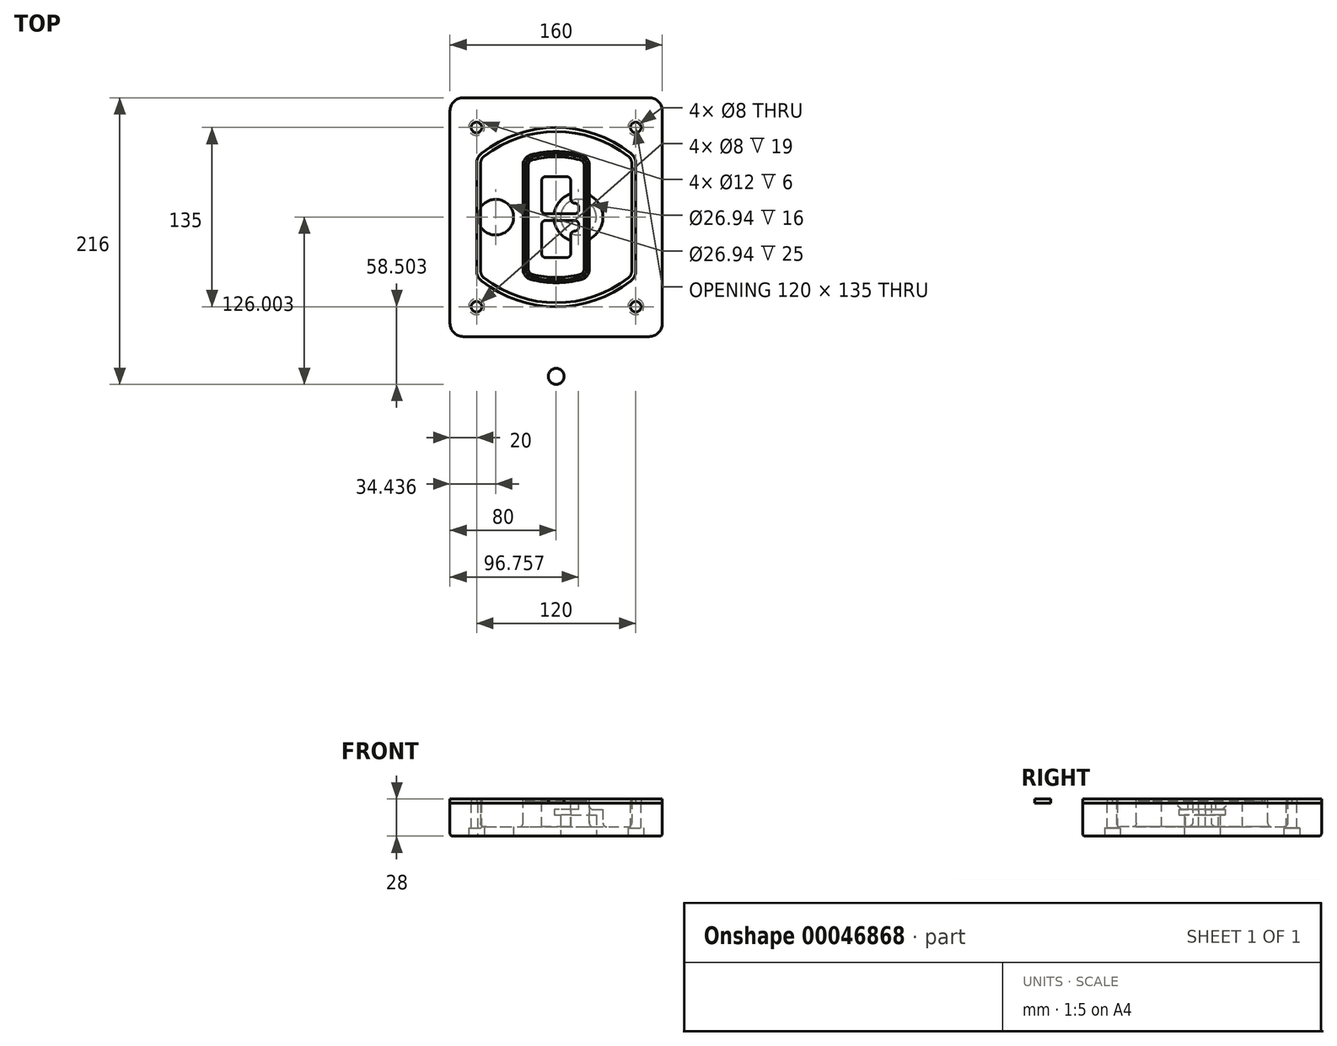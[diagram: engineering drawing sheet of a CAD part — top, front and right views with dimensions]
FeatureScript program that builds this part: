
annotation { "Feature Type Name" : "Feature", "Feature Type Description" : "" }
export const myFeature = defineFeature(function(context is Context, id is Id, definition is map)
    precondition{}
    {
        {
            var Q0;
            Q0=qCreatedBy(makeId("Top.planeOp"),FACE);
            var sketch = newSketch(context, id + "F0", { "sketchPlane" : qUnion([Q0])});
            skPoint(sketch, "E0.rect.middle", {"position": v(0, 0) * mm});
            skLineSegment(sketch, "E1.bottom", {"start": v(24.05, 28.38) * mm, "end": v(164.05, 28.38) * mm});
            skLineSegment(sketch, "E1.top", {"start": v(24.05, 208.38) * mm, "end": v(164.05, 208.38) * mm});
            skLineSegment(sketch, "E1.left", {"start": v(14.05, 38.38) * mm, "end": v(14.05, 198.38) * mm});
            skLineSegment(sketch, "E1.right", {"start": v(174.05, 38.38) * mm, "end": v(174.05, 198.38) * mm});
            skLineSegment(sketch, "E2", {"start": v(14.05, 208.38) * mm, "end": v(174.05, 28.38) * mm, "construction": true});
            skLineSegment(sketch, "E3", {"start": v(174.05, 208.38) * mm, "end": v(14.05, 28.38) * mm, "construction": true});
            skCircle(sketch, "E4", {"center": v(34.05, 185.88) * mm, "radius": 4 * mm});
            skCircle(sketch, "E5", {"center": v(154.05, 185.88) * mm, "radius": 4 * mm});
            skCircle(sketch, "E6", {"center": v(154.05, 50.88) * mm, "radius": 4 * mm});
            skCircle(sketch, "E7", {"center": v(34.05, 50.88) * mm, "radius": 4 * mm});
            skLineSegment(sketch, "E8", {"start": v(34.05, 185.88) * mm, "end": v(154.05, 185.88) * mm, "construction": true});
            skLineSegment(sketch, "E9", {"start": v(154.05, 185.88) * mm, "end": v(154.05, 50.88) * mm, "construction": true});
            skLineSegment(sketch, "E10", {"start": v(154.05, 50.88) * mm, "end": v(34.05, 50.88) * mm, "construction": true});
            skLineSegment(sketch, "E11", {"start": v(34.05, 50.88) * mm, "end": v(34.05, 185.88) * mm, "construction": true});
            skLineSegment(sketch, "E12", {"start": v(34.05, 158.68) * mm, "end": v(34.05, 78.09) * mm});
            skLineSegment(sketch, "E13", {"start": v(154.05, 158.68) * mm, "end": v(154.05, 78.09) * mm});
            skArc(sketch, "E14", {"start": v(150.2, 166.56) * mm, "mid": v(94.05, 185.88) * mm, "end": v(37.9, 166.56) * mm});
            skArc(sketch, "E15", {"start": v(37.9, 70.2) * mm, "mid": v(94.05, 50.88) * mm, "end": v(150.2, 70.2) * mm});
            skLineSegment(sketch, "E16", {"start": v(34.05, 118.38) * mm, "end": v(154.05, 118.38) * mm, "construction": true});
            skPoint(sketch, "E17.visualSharp", {"position": v(34.05, 73.38) * mm});
            skArc(sketch, "E17.filletArc", {"start": v(34.05, 78.09) * mm, "mid": v(35.06, 73.7) * mm, "end": v(37.9, 70.2) * mm});
            skPoint(sketch, "E18.visualSharp", {"position": v(34.05, 163.38) * mm});
            skArc(sketch, "E18.filletArc", {"start": v(37.9, 166.56) * mm, "mid": v(35.06, 163.06) * mm, "end": v(34.05, 158.68) * mm});
            skPoint(sketch, "E19.visualSharp", {"position": v(154.05, 163.38) * mm});
            skArc(sketch, "E19.filletArc", {"start": v(154.05, 158.68) * mm, "mid": v(153.04, 163.06) * mm, "end": v(150.2, 166.56) * mm});
            skPoint(sketch, "E20.visualSharp", {"position": v(154.05, 73.38) * mm});
            skArc(sketch, "E20.filletArc", {"start": v(150.2, 70.2) * mm, "mid": v(153.04, 73.7) * mm, "end": v(154.05, 78.09) * mm});
            skPoint(sketch, "E21.visualSharp", {"position": v(14.05, 208.38) * mm});
            skArc(sketch, "E21.filletArc", {"start": v(24.05, 208.38) * mm, "mid": v(16.98, 205.45) * mm, "end": v(14.05, 198.38) * mm});
            skPoint(sketch, "E22.visualSharp", {"position": v(174.05, 208.38) * mm});
            skArc(sketch, "E22.filletArc", {"start": v(174.05, 198.38) * mm, "mid": v(171.12, 205.45) * mm, "end": v(164.05, 208.38) * mm});
            skPoint(sketch, "E23.visualSharp", {"position": v(174.05, 28.38) * mm});
            skArc(sketch, "E23.filletArc", {"start": v(164.05, 28.38) * mm, "mid": v(171.12, 31.31) * mm, "end": v(174.05, 38.38) * mm});
            skPoint(sketch, "E24.visualSharp", {"position": v(14.05, 28.38) * mm});
            skArc(sketch, "E24.filletArc", {"start": v(14.05, 38.38) * mm, "mid": v(16.98, 31.31) * mm, "end": v(24.05, 28.38) * mm});
            skArc(sketch, "E25.0", {"start": v(151.05, 158.68) * mm, "mid": v(150.34, 161.75) * mm, "end": v(148.36, 164.2) * mm});
            skLineSegment(sketch, "E25.1", {"start": v(151.05, 158.68) * mm, "end": v(151.05, 78.09) * mm});
            skArc(sketch, "E25.2", {"start": v(148.36, 72.57) * mm, "mid": v(150.34, 75.02) * mm, "end": v(151.05, 78.09) * mm});
            skArc(sketch, "E25.3", {"start": v(39.74, 72.57) * mm, "mid": v(94.05, 53.88) * mm, "end": v(148.36, 72.57) * mm});
            skArc(sketch, "E25.4", {"start": v(37.05, 78.09) * mm, "mid": v(37.76, 75.02) * mm, "end": v(39.74, 72.57) * mm});
            skArc(sketch, "E25.5", {"start": v(148.36, 164.2) * mm, "mid": v(94.05, 182.88) * mm, "end": v(39.74, 164.2) * mm});
            skLineSegment(sketch, "E25.6", {"start": v(37.05, 158.68) * mm, "end": v(37.05, 78.09) * mm});
            skArc(sketch, "E25.7", {"start": v(39.74, 164.2) * mm, "mid": v(37.76, 161.75) * mm, "end": v(37.05, 158.68) * mm});
            skArc(sketch, "E26.0", {"start": v(35.43, 169.71) * mm, "mid": v(31.47, 164.82) * mm, "end": v(30.05, 158.68) * mm});
            skArc(sketch, "E26.1", {"start": v(152.67, 169.71) * mm, "mid": v(94.05, 189.88) * mm, "end": v(35.43, 169.71) * mm});
            skArc(sketch, "E26.2", {"start": v(158.05, 158.68) * mm, "mid": v(156.63, 164.82) * mm, "end": v(152.67, 169.71) * mm});
            skLineSegment(sketch, "E26.3", {"start": v(158.05, 158.68) * mm, "end": v(158.05, 78.09) * mm});
            skArc(sketch, "E26.4", {"start": v(152.67, 67.05) * mm, "mid": v(156.63, 71.95) * mm, "end": v(158.05, 78.09) * mm});
            skLineSegment(sketch, "E26.5", {"start": v(30.05, 158.68) * mm, "end": v(30.05, 78.09) * mm});
            skArc(sketch, "E26.6", {"start": v(35.43, 67.05) * mm, "mid": v(94.05, 46.88) * mm, "end": v(152.67, 67.05) * mm});
            skArc(sketch, "E26.7", {"start": v(30.05, 78.09) * mm, "mid": v(31.47, 71.95) * mm, "end": v(35.43, 67.05) * mm});
            skSolve(sketch);
        }
        {
            var Q0;
            Q0=makeQuery(id+"F0.imprint","IMPRINT",FACE,{"disambiguationData":[TD([[makeQuery(id+"F0.imprint","IMPRINT",EDGE,{"derivedFrom":sQuery(id+"F0.wireOp",EDGE,"E1.bottom")}),1.0]])]});
            var Q1;
            Q1=makeQuery(id+"F0.imprint","IMPRINT",FACE,{"disambiguationData":[TD([[makeQuery(id+"F0.imprint","IMPRINT",EDGE,{"derivedFrom":sQuery(id+"F0.wireOp",EDGE,"E12")}),1.0]])]});
            var Q2;
            Q2=makeQuery(id+"F0.imprint","IMPRINT",FACE,{"disambiguationData":[TD([[makeQuery(id+"F0.imprint","IMPRINT",EDGE,{"derivedFrom":sQuery(id+"F0.wireOp",EDGE,"E25.0")}),1.0]])]});
            var Q3;
            Q3=makeQuery(id+"F0.imprint","IMPRINT",FACE,{"disambiguationData":[TD([[makeQuery(id+"F0.imprint","IMPRINT",EDGE,{"derivedFrom":sQuery(id+"F0.wireOp",EDGE,"E12")}),-1.0]])]});
            extrude(context, id + "F1", {"entities" : qUnion([Q0, Q1, Q2, Q3]), "oppositeDirection" : true, "depth" : 25 * mm});
        }
        {
            var Q0;
            Q0=makeQuery(id+"F0.imprint","IMPRINT",FACE,{"disambiguationData":[TD([[makeQuery(id+"F0.imprint","IMPRINT",EDGE,{"derivedFrom":sQuery(id+"F0.wireOp",EDGE,"E12")}),1.0]])]});
            extrude(context, id + "F2", {"entities" : qUnion([Q0]), "operationType" : NewBodyOperationType.ADD, "depth" : 3 * mm});
        }
        {
            var Q0;
            Q0=makeQuery(id+"F0.imprint","IMPRINT",FACE,{"disambiguationData":[TD([[makeQuery(id+"F0.imprint","IMPRINT",EDGE,{"derivedFrom":sQuery(id+"F0.wireOp",EDGE,"E25.0")}),1.0]])]});
            extrude(context, id + "F3", {"entities" : qUnion([Q0]), "operationType" : NewBodyOperationType.REMOVE, "oppositeDirection" : true, "depth" : 18 * mm});
        }
        {
            var Q0;
            Q0=makeQuery(id+"F2.opExtrude","CAP_FACE",FACE,{"disambiguationData":[OSD([sQuery(id+"F0.wireOp",EDGE,"E12"),sQuery(id+"F0.wireOp",EDGE,"E13"),sQuery(id+"F0.wireOp",EDGE,"E14"),sQuery(id+"F0.wireOp",EDGE,"E15"),sQuery(id+"F0.wireOp",EDGE,"E17.filletArc"),sQuery(id+"F0.wireOp",EDGE,"E18.filletArc"),sQuery(id+"F0.wireOp",EDGE,"E19.filletArc"),sQuery(id+"F0.wireOp",EDGE,"E20.filletArc"),sQuery(id+"F0.wireOp",EDGE,"E25.0"),sQuery(id+"F0.wireOp",EDGE,"E25.1"),sQuery(id+"F0.wireOp",EDGE,"E25.2"),sQuery(id+"F0.wireOp",EDGE,"E25.3"),sQuery(id+"F0.wireOp",EDGE,"E25.4"),sQuery(id+"F0.wireOp",EDGE,"E25.5"),sQuery(id+"F0.wireOp",EDGE,"E25.6"),sQuery(id+"F0.wireOp",EDGE,"E25.7")])],"isStart":false});
            var sketch = newSketch(context, id + "F4", { "sketchPlane" : qUnion([Q0])});
            skArc(sketch, "E27.0", {"start": v(74.97, 71.41) * mm, "mid": v(94.05, 68.88) * mm, "end": v(113.13, 71.41) * mm});
            skArc(sketch, "E28.0", {"start": v(113.13, 165.35) * mm, "mid": v(94.05, 167.88) * mm, "end": v(74.97, 165.35) * mm});
            skLineSegment(sketch, "E29", {"start": v(69.05, 157.63) * mm, "end": v(69.05, 79.14) * mm});
            skLineSegment(sketch, "E30", {"start": v(119.05, 157.63) * mm, "end": v(119.05, 79.14) * mm});
            skLineSegment(sketch, "E31", {"start": v(69.05, 163.48) * mm, "end": v(119.05, 163.48) * mm, "construction": true});
            skLineSegment(sketch, "E32", {"start": v(69.05, 73.28) * mm, "end": v(119.05, 73.28) * mm, "construction": true});
            skPoint(sketch, "E33.visualSharp", {"position": v(69.05, 163.48) * mm});
            skArc(sketch, "E33.filletArc", {"start": v(74.97, 165.35) * mm, "mid": v(70.7, 162.5) * mm, "end": v(69.05, 157.63) * mm});
            skPoint(sketch, "E34.visualSharp", {"position": v(119.05, 163.48) * mm});
            skArc(sketch, "E34.filletArc", {"start": v(119.05, 157.63) * mm, "mid": v(117.4, 162.5) * mm, "end": v(113.13, 165.35) * mm});
            skPoint(sketch, "E35.visualSharp", {"position": v(119.05, 73.28) * mm});
            skArc(sketch, "E35.filletArc", {"start": v(113.13, 71.41) * mm, "mid": v(117.4, 74.27) * mm, "end": v(119.05, 79.14) * mm});
            skPoint(sketch, "E36.visualSharp", {"position": v(69.05, 73.28) * mm});
            skArc(sketch, "E36.filletArc", {"start": v(69.05, 79.14) * mm, "mid": v(70.7, 74.27) * mm, "end": v(74.97, 71.41) * mm});
            skArc(sketch, "E37.0", {"start": v(148.36, 164.2) * mm, "mid": v(94.05, 182.88) * mm, "end": v(39.74, 164.2) * mm});
            skArc(sketch, "E37.1", {"start": v(39.74, 164.2) * mm, "mid": v(37.76, 161.75) * mm, "end": v(37.05, 158.68) * mm});
            skLineSegment(sketch, "E37.2", {"start": v(37.05, 158.68) * mm, "end": v(37.05, 78.09) * mm});
            skArc(sketch, "E37.3", {"start": v(37.05, 78.09) * mm, "mid": v(37.76, 75.02) * mm, "end": v(39.74, 72.57) * mm});
            skArc(sketch, "E37.4", {"start": v(39.74, 72.57) * mm, "mid": v(94.05, 53.88) * mm, "end": v(148.36, 72.57) * mm});
            skArc(sketch, "E37.5", {"start": v(148.36, 72.57) * mm, "mid": v(150.34, 75.02) * mm, "end": v(151.05, 78.09) * mm});
            skLineSegment(sketch, "E37.6", {"start": v(151.05, 158.68) * mm, "end": v(151.05, 78.09) * mm});
            skArc(sketch, "E37.7", {"start": v(151.05, 158.68) * mm, "mid": v(150.34, 161.75) * mm, "end": v(148.36, 164.2) * mm});
            skLineSegment(sketch, "E38.0", {"start": v(117.05, 157.63) * mm, "end": v(117.05, 79.14) * mm});
            skArc(sketch, "E38.1", {"start": v(112.61, 73.34) * mm, "mid": v(115.81, 75.49) * mm, "end": v(117.05, 79.14) * mm});
            skArc(sketch, "E38.2", {"start": v(75.49, 73.34) * mm, "mid": v(94.05, 70.88) * mm, "end": v(112.61, 73.34) * mm});
            skArc(sketch, "E38.3", {"start": v(71.05, 79.14) * mm, "mid": v(72.29, 75.49) * mm, "end": v(75.49, 73.34) * mm});
            skLineSegment(sketch, "E38.4", {"start": v(71.05, 157.63) * mm, "end": v(71.05, 79.14) * mm});
            skArc(sketch, "E38.5", {"start": v(117.05, 157.63) * mm, "mid": v(115.81, 161.28) * mm, "end": v(112.61, 163.42) * mm});
            skArc(sketch, "E38.6", {"start": v(75.49, 163.42) * mm, "mid": v(72.29, 161.28) * mm, "end": v(71.05, 157.63) * mm});
            skArc(sketch, "E38.7", {"start": v(112.61, 163.42) * mm, "mid": v(94.05, 165.88) * mm, "end": v(75.49, 163.42) * mm});
            skArc(sketch, "E39.0", {"start": v(115.05, 157.63) * mm, "mid": v(114.23, 160.06) * mm, "end": v(112.1, 161.5) * mm});
            skLineSegment(sketch, "E39.1", {"start": v(115.05, 157.63) * mm, "end": v(115.05, 79.14) * mm});
            skArc(sketch, "E39.2", {"start": v(112.1, 75.27) * mm, "mid": v(114.23, 76.7) * mm, "end": v(115.05, 79.14) * mm});
            skArc(sketch, "E39.3", {"start": v(76, 75.27) * mm, "mid": v(94.05, 72.88) * mm, "end": v(112.1, 75.27) * mm});
            skArc(sketch, "E39.4", {"start": v(73.05, 79.14) * mm, "mid": v(73.87, 76.7) * mm, "end": v(76, 75.27) * mm});
            skArc(sketch, "E39.5", {"start": v(112.1, 161.5) * mm, "mid": v(94.05, 163.88) * mm, "end": v(76, 161.5) * mm});
            skLineSegment(sketch, "E39.6", {"start": v(73.05, 157.63) * mm, "end": v(73.05, 79.14) * mm});
            skArc(sketch, "E39.7", {"start": v(76, 161.5) * mm, "mid": v(73.87, 160.06) * mm, "end": v(73.05, 157.63) * mm});
            skLineSegment(sketch, "E40", {"start": v(69.05, 118.38) * mm, "end": v(119.05, 118.38) * mm, "construction": true});
            skLineSegment(sketch, "E41", {"start": v(83.05, 123.88) * mm, "end": v(83.05, 145.88) * mm});
            skLineSegment(sketch, "E42", {"start": v(86.05, 148.88) * mm, "end": v(102.05, 148.88) * mm});
            skLineSegment(sketch, "E43", {"start": v(105.05, 145.88) * mm, "end": v(105.05, 131.88) * mm});
            skLineSegment(sketch, "E44", {"start": v(108.05, 128.88) * mm, "end": v(108.05, 128.88) * mm});
            skLineSegment(sketch, "E45", {"start": v(111.05, 125.88) * mm, "end": v(111.05, 123.88) * mm});
            skLineSegment(sketch, "E46", {"start": v(108.05, 120.88) * mm, "end": v(86.05, 120.88) * mm});
            skPoint(sketch, "E47.visualSharp", {"position": v(83.05, 148.88) * mm});
            skArc(sketch, "E47.filletArc", {"start": v(86.05, 148.88) * mm, "mid": v(83.93, 148) * mm, "end": v(83.05, 145.88) * mm});
            skPoint(sketch, "E48.visualSharp", {"position": v(105.05, 148.88) * mm});
            skArc(sketch, "E48.filletArc", {"start": v(105.05, 145.88) * mm, "mid": v(104.17, 148) * mm, "end": v(102.05, 148.88) * mm});
            skPoint(sketch, "E49.visualSharp", {"position": v(105.05, 128.88) * mm});
            skArc(sketch, "E49.filletArc", {"start": v(105.05, 131.88) * mm, "mid": v(105.93, 129.76) * mm, "end": v(108.05, 128.88) * mm});
            skPoint(sketch, "E50.visualSharp", {"position": v(111.05, 128.88) * mm});
            skArc(sketch, "E50.filletArc", {"start": v(111.05, 125.88) * mm, "mid": v(110.17, 128) * mm, "end": v(108.05, 128.88) * mm});
            skPoint(sketch, "E51.visualSharp", {"position": v(111.05, 120.88) * mm});
            skArc(sketch, "E51.filletArc", {"start": v(108.05, 120.88) * mm, "mid": v(110.17, 121.76) * mm, "end": v(111.05, 123.88) * mm});
            skPoint(sketch, "E52.visualSharp", {"position": v(83.05, 120.88) * mm});
            skArc(sketch, "E52.filletArc", {"start": v(83.05, 123.88) * mm, "mid": v(83.93, 121.76) * mm, "end": v(86.05, 120.88) * mm});
            skLineSegment(sketch, "E53.0.MirrorCS", {"start": v(108.05, 115.88) * mm, "end": v(86.05, 115.88) * mm});
            skArc(sketch, "E54.0.MirrorCS", {"start": v(83.05, 112.88) * mm, "mid": v(83.93, 115) * mm, "end": v(86.05, 115.88) * mm});
            skLineSegment(sketch, "E55.0.MirrorCS", {"start": v(83.05, 112.88) * mm, "end": v(83.05, 90.88) * mm});
            skArc(sketch, "E56.0.MirrorCS", {"start": v(86.05, 87.88) * mm, "mid": v(83.93, 88.76) * mm, "end": v(83.05, 90.88) * mm});
            skLineSegment(sketch, "E57.0.MirrorCS", {"start": v(86.05, 87.88) * mm, "end": v(102.05, 87.88) * mm});
            skArc(sketch, "E58.0.MirrorCS", {"start": v(105.05, 90.88) * mm, "mid": v(104.17, 88.76) * mm, "end": v(102.05, 87.88) * mm});
            skLineSegment(sketch, "E59.0.MirrorCS", {"start": v(105.05, 90.88) * mm, "end": v(105.05, 104.88) * mm});
            skArc(sketch, "E60.0.MirrorCS", {"start": v(105.05, 104.88) * mm, "mid": v(105.93, 107) * mm, "end": v(108.05, 107.88) * mm});
            skArc(sketch, "E61.0.MirrorCS", {"start": v(111.05, 110.88) * mm, "mid": v(110.17, 108.76) * mm, "end": v(108.05, 107.88) * mm});
            skLineSegment(sketch, "E62.0.MirrorCS", {"start": v(111.05, 110.88) * mm, "end": v(111.05, 112.88) * mm});
            skArc(sketch, "E63.0.MirrorCS", {"start": v(108.05, 115.88) * mm, "mid": v(110.17, 115) * mm, "end": v(111.05, 112.88) * mm});
            skSolve(sketch);
        }
        {
            var Q0;
            Q0=makeQuery(id+"F4.imprint","IMPRINT",FACE,{"disambiguationData":[TD([[makeQuery(id+"F4.imprint","IMPRINT",EDGE,{"derivedFrom":sQuery(id+"F4.wireOp",EDGE,"E27.0")}),1.0]])]});
            var Q1;
            Q1=makeQuery(id+"F4.imprint","IMPRINT",FACE,{"disambiguationData":[TD([[makeQuery(id+"F4.imprint","IMPRINT",EDGE,{"derivedFrom":sQuery(id+"F4.wireOp",EDGE,"E38.0")}),-1.0]])]});
            var Q2;
            Q2=makeQuery(id+"F4.imprint","IMPRINT",FACE,{"disambiguationData":[TD([[makeQuery(id+"F4.imprint","IMPRINT",EDGE,{"derivedFrom":sQuery(id+"F4.wireOp",EDGE,"E39.0")}),1.0]])]});
            extrude(context, id + "F5", {"entities" : qUnion([Q0, Q1, Q2]), "operationType" : NewBodyOperationType.ADD, "endBound" : BoundingType.UP_TO_NEXT, "oppositeDirection" : true, "depth" : 25 * mm});
        }
        {
            var Q0;
            Q0=makeQuery(id+"F4.imprint","IMPRINT",FACE,{"disambiguationData":[TD([[makeQuery(id+"F4.imprint","IMPRINT",EDGE,{"derivedFrom":sQuery(id+"F4.wireOp",EDGE,"E38.0")}),-1.0]])]});
            extrude(context, id + "F6", {"entities" : qUnion([Q0]), "operationType" : NewBodyOperationType.REMOVE, "oppositeDirection" : true, "depth" : 2 * mm});
        }
        {
            var Q0;
            Q0=makeQuery(id+"F1.opExtrude","CAP_FACE",FACE,{"disambiguationData":[OSD([sQuery(id+"F0.wireOp",EDGE,"E1.bottom"),sQuery(id+"F0.wireOp",EDGE,"E1.top"),sQuery(id+"F0.wireOp",EDGE,"E1.left"),sQuery(id+"F0.wireOp",EDGE,"E1.right"),sQuery(id+"F0.wireOp",EDGE,"E4"),sQuery(id+"F0.wireOp",EDGE,"E5"),sQuery(id+"F0.wireOp",EDGE,"E6"),sQuery(id+"F0.wireOp",EDGE,"E7"),sQuery(id+"F0.wireOp",EDGE,"E21.filletArc"),sQuery(id+"F0.wireOp",EDGE,"E22.filletArc"),sQuery(id+"F0.wireOp",EDGE,"E23.filletArc"),sQuery(id+"F0.wireOp",EDGE,"E24.filletArc")])],"isStart":false});
            var sketch = newSketch(context, id + "F7", { "sketchPlane" : qUnion([Q0])});
            skCircle(sketch, "E64", {"center": v(110.8, -118.38) * mm, "radius": 13.47 * mm});
            skCircle(sketch, "E65", {"center": v(48.49, -118.38) * mm, "radius": 13.47 * mm});
            skLineSegment(sketch, "E66", {"start": v(174.05, -118.38) * mm, "end": v(14.05, -118.38) * mm});
            skCircle(sketch, "E67", {"center": v(110.8, -118.38) * mm, "radius": 18.47 * mm});
            skCircle(sketch, "E68", {"center": v(154.05, -185.88) * mm, "radius": 6 * mm});
            skCircle(sketch, "E69", {"center": v(34.05, -185.88) * mm, "radius": 6 * mm});
            skCircle(sketch, "E70", {"center": v(34.05, -50.88) * mm, "radius": 6 * mm});
            skCircle(sketch, "E71", {"center": v(154.05, -50.88) * mm, "radius": 6 * mm});
            skSolve(sketch);
        }
        {
            var Q0;
            {var subQ1=sQuery(id+"F7.wireOp",EDGE,"E66");var subQ4=sQuery(id+"F7.wireOp",EDGE,"E64");var subQ6=makeQuery(id+"F7.imprint","INTERSECT",VERTEX,{"disambiguationData":[OD(0.0)],"derivedFrom":[subQ4,subQ1]});Q0=makeQuery(id+"F7.imprint","IMPRINT",FACE,{"disambiguationData":[TD([[makeQuery(id+"F7.imprint","IMPRINT",EDGE,{"disambiguationData":[TD([[subQ6,-1.0]])],"derivedFrom":subQ4}),-1.0]])]});}
            var Q1;
            {var subQ0=sQuery(id+"F7.wireOp",EDGE,"E66");var subQ1=sQuery(id+"F7.wireOp",EDGE,"E64");var subQ3=makeQuery(id+"F7.imprint","INTERSECT",VERTEX,{"disambiguationData":[OD(0.0)],"derivedFrom":[subQ1,subQ0]});Q1=makeQuery(id+"F7.imprint","IMPRINT",FACE,{"disambiguationData":[TD([[makeQuery(id+"F7.imprint","IMPRINT",EDGE,{"disambiguationData":[TD([[subQ3,-1.0]])],"derivedFrom":subQ1}),1.0]])]});}
            var Q2;
            {var subQ0=sQuery(id+"F7.wireOp",EDGE,"E66");var subQ1=sQuery(id+"F7.wireOp",EDGE,"E64");var subQ3=makeQuery(id+"F7.imprint","INTERSECT",VERTEX,{"disambiguationData":[OD(0.0)],"derivedFrom":[subQ1,subQ0]});Q2=makeQuery(id+"F7.imprint","IMPRINT",FACE,{"disambiguationData":[TD([[makeQuery(id+"F7.imprint","IMPRINT",EDGE,{"disambiguationData":[TD([[subQ3,1.0]])],"derivedFrom":subQ1}),1.0]])]});}
            var Q3;
            {var subQ1=sQuery(id+"F7.wireOp",EDGE,"E66");var subQ4=sQuery(id+"F7.wireOp",EDGE,"E64");var subQ6=makeQuery(id+"F7.imprint","INTERSECT",VERTEX,{"disambiguationData":[OD(0.0)],"derivedFrom":[subQ4,subQ1]});Q3=makeQuery(id+"F7.imprint","IMPRINT",FACE,{"disambiguationData":[TD([[makeQuery(id+"F7.imprint","IMPRINT",EDGE,{"disambiguationData":[TD([[subQ6,1.0]])],"derivedFrom":subQ4}),-1.0]])]});}
            extrude(context, id + "F8", {"entities" : qUnion([Q0, Q1, Q2, Q3]), "operationType" : NewBodyOperationType.ADD, "oppositeDirection" : true, "depth" : 20 * mm});
        }
        {
            var Q0;
            {var subQ0=sQuery(id+"F7.wireOp",EDGE,"E66");var subQ1=sQuery(id+"F7.wireOp",EDGE,"E64");var subQ3=makeQuery(id+"F7.imprint","INTERSECT",VERTEX,{"disambiguationData":[OD(0.0)],"derivedFrom":[subQ1,subQ0]});Q0=makeQuery(id+"F7.imprint","IMPRINT",FACE,{"disambiguationData":[TD([[makeQuery(id+"F7.imprint","IMPRINT",EDGE,{"disambiguationData":[TD([[subQ3,-1.0]])],"derivedFrom":subQ1}),1.0]])]});}
            var Q1;
            {var subQ0=sQuery(id+"F7.wireOp",EDGE,"E66");var subQ1=sQuery(id+"F7.wireOp",EDGE,"E64");var subQ3=makeQuery(id+"F7.imprint","INTERSECT",VERTEX,{"disambiguationData":[OD(0.0)],"derivedFrom":[subQ1,subQ0]});Q1=makeQuery(id+"F7.imprint","IMPRINT",FACE,{"disambiguationData":[TD([[makeQuery(id+"F7.imprint","IMPRINT",EDGE,{"disambiguationData":[TD([[subQ3,1.0]])],"derivedFrom":subQ1}),1.0]])]});}
            extrude(context, id + "F9", {"entities" : qUnion([Q0, Q1]), "operationType" : NewBodyOperationType.REMOVE, "oppositeDirection" : true, "depth" : 16 * mm});
        }
        {
            var Q0;
            {var subQ0=sQuery(id+"F7.wireOp",EDGE,"E66");var subQ1=sQuery(id+"F7.wireOp",EDGE,"E65");var subQ3=makeQuery(id+"F7.imprint","INTERSECT",VERTEX,{"disambiguationData":[OD(0.0)],"derivedFrom":[subQ1,subQ0]});Q0=makeQuery(id+"F7.imprint","IMPRINT",FACE,{"disambiguationData":[TD([[makeQuery(id+"F7.imprint","IMPRINT",EDGE,{"disambiguationData":[TD([[subQ3,-1.0]])],"derivedFrom":subQ1}),1.0]])]});}
            var Q1;
            {var subQ0=sQuery(id+"F7.wireOp",EDGE,"E66");var subQ1=sQuery(id+"F7.wireOp",EDGE,"E65");var subQ3=makeQuery(id+"F7.imprint","INTERSECT",VERTEX,{"disambiguationData":[OD(0.0)],"derivedFrom":[subQ1,subQ0]});Q1=makeQuery(id+"F7.imprint","IMPRINT",FACE,{"disambiguationData":[TD([[makeQuery(id+"F7.imprint","IMPRINT",EDGE,{"disambiguationData":[TD([[subQ3,1.0]])],"derivedFrom":subQ1}),1.0]])]});}
            extrude(context, id + "F10", {"entities" : qUnion([Q0, Q1]), "operationType" : NewBodyOperationType.REMOVE, "oppositeDirection" : true, "depth" : 25 * mm});
        }
        {
            var Q0;
            Q0=makeQuery(id+"F7.imprint","IMPRINT",FACE,{"disambiguationData":[TD([[makeQuery(id+"F7.imprint","IMPRINT",EDGE,{"derivedFrom":sQuery(id+"F7.wireOp",EDGE,"E68")}),1.0]])]});
            var Q1;
            Q1=makeQuery(id+"F7.imprint","IMPRINT",FACE,{"disambiguationData":[TD([[makeQuery(id+"F7.imprint","IMPRINT",EDGE,{"derivedFrom":makeQuery(id+"F1.opExtrude","CAP_EDGE",EDGE,{"disambiguationData":[OSD([sQuery(id+"F0.wireOp",EDGE,"E5")])],"isStart":false})}),-1.0]])]});
            var Q2;
            Q2=makeQuery(id+"F7.imprint","IMPRINT",FACE,{"disambiguationData":[TD([[makeQuery(id+"F7.imprint","IMPRINT",EDGE,{"derivedFrom":sQuery(id+"F7.wireOp",EDGE,"E69")}),1.0]])]});
            var Q3;
            Q3=makeQuery(id+"F7.imprint","IMPRINT",FACE,{"disambiguationData":[TD([[makeQuery(id+"F7.imprint","IMPRINT",EDGE,{"derivedFrom":makeQuery(id+"F1.opExtrude","CAP_EDGE",EDGE,{"disambiguationData":[OSD([sQuery(id+"F0.wireOp",EDGE,"E4")])],"isStart":false})}),-1.0]])]});
            var Q4;
            Q4=makeQuery(id+"F7.imprint","IMPRINT",FACE,{"disambiguationData":[TD([[makeQuery(id+"F7.imprint","IMPRINT",EDGE,{"derivedFrom":sQuery(id+"F7.wireOp",EDGE,"E70")}),1.0]])]});
            var Q5;
            Q5=makeQuery(id+"F7.imprint","IMPRINT",FACE,{"disambiguationData":[TD([[makeQuery(id+"F7.imprint","IMPRINT",EDGE,{"derivedFrom":makeQuery(id+"F1.opExtrude","CAP_EDGE",EDGE,{"disambiguationData":[OSD([sQuery(id+"F0.wireOp",EDGE,"E7")])],"isStart":false})}),-1.0]])]});
            var Q6;
            Q6=makeQuery(id+"F7.imprint","IMPRINT",FACE,{"disambiguationData":[TD([[makeQuery(id+"F7.imprint","IMPRINT",EDGE,{"derivedFrom":sQuery(id+"F7.wireOp",EDGE,"E71")}),1.0]])]});
            var Q7;
            Q7=makeQuery(id+"F7.imprint","IMPRINT",FACE,{"disambiguationData":[TD([[makeQuery(id+"F7.imprint","IMPRINT",EDGE,{"derivedFrom":makeQuery(id+"F1.opExtrude","CAP_EDGE",EDGE,{"disambiguationData":[OSD([sQuery(id+"F0.wireOp",EDGE,"E6")])],"isStart":false})}),-1.0]])]});
            extrude(context, id + "F11", {"entities" : qUnion([Q0, Q1, Q2, Q3, Q4, Q5, Q6, Q7]), "operationType" : NewBodyOperationType.REMOVE, "oppositeDirection" : true, "depth" : 6 * mm});
        }
        {
            var Q0;
            Q0=makeQuery(id+"F9.boolean.opBoolean","COPY",FACE,{"derivedFrom":makeQuery(id+"F9.opExtrude","CAP_FACE",FACE,{"disambiguationData":[OSD([sQuery(id+"F7.wireOp",EDGE,"E64")])],"isStart":false})});
            var sketch = newSketch(context, id + "F12", { "sketchPlane" : qUnion([Q0])});
            skArc(sketch, "E72.0", {"start": v(105.05, -100.83) * mm, "mid": v(96.62, -106.56) * mm, "end": v(92.5, -115.88) * mm});
            skArc(sketch, "E72.1", {"start": v(92.5, -120.88) * mm, "mid": v(96.62, -130.2) * mm, "end": v(105.05, -135.93) * mm});
            skLineSegment(sketch, "E73", {"start": v(92.5, -120.88) * mm, "end": v(108.05, -120.88) * mm});
            skLineSegment(sketch, "E74.0", {"start": v(108.05, -115.88) * mm, "end": v(92.5, -115.88) * mm});
            skArc(sketch, "E74.1", {"start": v(108.05, -115.88) * mm, "mid": v(110.17, -115) * mm, "end": v(111.05, -112.88) * mm});
            skLineSegment(sketch, "E74.2", {"start": v(111.05, -110.88) * mm, "end": v(111.05, -112.88) * mm});
            skArc(sketch, "E74.3", {"start": v(111.05, -110.88) * mm, "mid": v(110.17, -108.76) * mm, "end": v(108.05, -107.88) * mm});
            skArc(sketch, "E74.4", {"start": v(105.05, -104.88) * mm, "mid": v(105.93, -107) * mm, "end": v(108.05, -107.88) * mm});
            skLineSegment(sketch, "E74.5", {"start": v(105.05, -100.83) * mm, "end": v(105.05, -104.88) * mm});
            skLineSegment(sketch, "E74.7", {"start": v(108.05, -120.88) * mm, "end": v(92.5, -120.88) * mm});
            skArc(sketch, "E74.8", {"start": v(108.05, -120.88) * mm, "mid": v(110.17, -121.76) * mm, "end": v(111.05, -123.88) * mm});
            skLineSegment(sketch, "E74.9", {"start": v(111.05, -125.88) * mm, "end": v(111.05, -123.88) * mm});
            skArc(sketch, "E74.10", {"start": v(111.05, -125.88) * mm, "mid": v(110.17, -128) * mm, "end": v(108.05, -128.88) * mm});
            skArc(sketch, "E74.11", {"start": v(105.05, -131.88) * mm, "mid": v(105.93, -129.76) * mm, "end": v(108.05, -128.88) * mm});
            skLineSegment(sketch, "E74.12", {"start": v(105.05, -135.93) * mm, "end": v(105.05, -131.88) * mm});
            skPoint(sketch, "E75.orphan", {"position": v(105.05, -145.88) * mm});
            skPoint(sketch, "E76.orphan", {"position": v(86.05, -120.88) * mm});
            skPoint(sketch, "E77.orphan", {"position": v(86.05, -115.88) * mm});
            skPoint(sketch, "E78.orphan", {"position": v(105.05, -90.88) * mm});
            skSolve(sketch);
        }
        {
            var Q0;
            {var subQ7=sQuery(id+"F12.wireOp",EDGE,"E72.0");var subQ14=sQuery(id+"F12.wireOp",EDGE,"E72.1");var subQ16=sQuery(id+"F12.wireOp",EDGE,"E74.1");var subQ18=sQuery(id+"F12.wireOp",EDGE,"E74.8");Q0=qUnion([makeQuery(id+"F12.imprint","IMPRINT",FACE,{"disambiguationData":[TD([[makeQuery(id+"F12.imprint","IMPRINT",EDGE,{"derivedFrom":subQ7}),1.0]])]}),makeQuery(id+"F12.imprint","IMPRINT",FACE,{"disambiguationData":[TD([[makeQuery(id+"F12.imprint","IMPRINT",EDGE,{"derivedFrom":subQ14}),1.0]])]}),makeQuery(id+"F12.imprint","IMPRINT",FACE,{"disambiguationData":[TD([[makeQuery(id+"F12.imprint","IMPRINT",EDGE,{"derivedFrom":subQ16}),1.0]])]}),makeQuery(id+"F12.imprint","IMPRINT",FACE,{"disambiguationData":[TD([[makeQuery(id+"F12.imprint","IMPRINT",EDGE,{"derivedFrom":subQ18}),-1.0]])]})]);}
            var Q1;
            Q1=makeQuery(id+"F5.boolean.opBoolean","SPLIT",FACE,{"disambiguationData":[TD([makeQuery(id+"F5.opExtrude","SWEPT_FACE",FACE,{"disambiguationData":[OSD([sQuery(id+"F4.wireOp",EDGE,"E41")])]})])],"derivedFrom":makeQuery(id+"F3.boolean.opBoolean","COPY",FACE,{"derivedFrom":makeQuery(id+"F3.opExtrude","CAP_FACE",FACE,{"disambiguationData":[OSD([sQuery(id+"F0.wireOp",EDGE,"E25.0"),sQuery(id+"F0.wireOp",EDGE,"E25.1"),sQuery(id+"F0.wireOp",EDGE,"E25.2"),sQuery(id+"F0.wireOp",EDGE,"E25.3"),sQuery(id+"F0.wireOp",EDGE,"E25.4"),sQuery(id+"F0.wireOp",EDGE,"E25.5"),sQuery(id+"F0.wireOp",EDGE,"E25.6"),sQuery(id+"F0.wireOp",EDGE,"E25.7")])],"isStart":false})})});
            extrude(context, id + "F13", {"entities" : qUnion([Q0]), "operationType" : NewBodyOperationType.REMOVE, "endBound" : BoundingType.UP_TO_SURFACE, "endBoundEntityFace" : qUnion([Q1]), "depth" : 25 * mm});
        }
        {
            var Q0;
            Q0=makeQuery(id+"F3.boolean.opBoolean","COPY",EDGE,{"derivedFrom":makeQuery(id+"F3.opExtrude","CAP_EDGE",EDGE,{"disambiguationData":[OSD([sQuery(id+"F0.wireOp",EDGE,"E25.6")])],"isStart":false})});
            var Q1;
            Q1=makeQuery(id+"F8.boolean.opBoolean","INTERSECT",EDGE,{"derivedFrom":[makeQuery(id+"F5.opExtrude","SWEPT_FACE",FACE,{"disambiguationData":[OSD([sQuery(id+"F4.wireOp",EDGE,"E30")])]}),makeQuery(id+"F8.opExtrude","CAP_FACE",FACE,{"disambiguationData":[OSD([sQuery(id+"F7.wireOp",EDGE,"E67")])],"isStart":false})]});
            var Q2;
            Q2=makeQuery(id+"F8.boolean.opBoolean","INTERSECT",EDGE,{"disambiguationData":[OD(1.0)],"derivedFrom":[makeQuery(id+"F5.opExtrude","SWEPT_FACE",FACE,{"disambiguationData":[OSD([sQuery(id+"F4.wireOp",EDGE,"E30")])]}),makeQuery(id+"F8.opExtrude","SWEPT_FACE",FACE,{"disambiguationData":[OSD([sQuery(id+"F7.wireOp",EDGE,"E67")])]})]});
            var Q3;
            {var subQ0=sQuery(id+"F4.wireOp",EDGE,"E30");Q3=makeQuery(id+"F8.boolean.opBoolean","SPLIT",EDGE,{"disambiguationData":[TD([makeQuery(id+"F5.opExtrude","SWEPT_FACE",FACE,{"disambiguationData":[OSD([sQuery(id+"F4.wireOp",EDGE,"E35.filletArc")])]})])],"derivedFrom":makeQuery(id+"F5.opExtrude","CAP_EDGE",EDGE,{"disambiguationData":[OSD([subQ0])],"isStart":false})});}
            var Q4;
            {var subQ0=sQuery(id+"F0.wireOp",EDGE,"E25.7");var subQ1=sQuery(id+"F0.wireOp",EDGE,"E25.1");var subQ2=sQuery(id+"F0.wireOp",EDGE,"E25.6");var subQ3=sQuery(id+"F0.wireOp",EDGE,"E25.5");var subQ4=sQuery(id+"F0.wireOp",EDGE,"E25.4");var subQ5=sQuery(id+"F0.wireOp",EDGE,"E25.0");var subQ6=sQuery(id+"F0.wireOp",EDGE,"E25.2");var subQ7=sQuery(id+"F0.wireOp",EDGE,"E25.3");Q4=makeQuery(id+"F8.boolean.opBoolean","INTERSECT",EDGE,{"derivedFrom":[makeQuery(id+"F5.boolean.opBoolean","SPLIT",FACE,{"disambiguationData":[TD([makeQuery(id+"F2.opExtrude","SWEPT_FACE",FACE,{"disambiguationData":[OSD([subQ5])]})])],"derivedFrom":makeQuery(id+"F3.boolean.opBoolean","COPY",FACE,{"derivedFrom":makeQuery(id+"F3.opExtrude","CAP_FACE",FACE,{"disambiguationData":[OSD([subQ5,subQ1,subQ6,subQ7,subQ4,subQ3,subQ2,subQ0])],"isStart":false})})}),makeQuery(id+"F8.opExtrude","SWEPT_FACE",FACE,{"disambiguationData":[OSD([sQuery(id+"F7.wireOp",EDGE,"E67")])]})]});}
            var Q5;
            Q5=makeQuery(id+"F8.boolean.opBoolean","INTERSECT",EDGE,{"disambiguationData":[OD(0.0)],"derivedFrom":[makeQuery(id+"F5.opExtrude","SWEPT_FACE",FACE,{"disambiguationData":[OSD([sQuery(id+"F4.wireOp",EDGE,"E30")])]}),makeQuery(id+"F8.opExtrude","SWEPT_FACE",FACE,{"disambiguationData":[OSD([sQuery(id+"F7.wireOp",EDGE,"E67")])]})]});
            fillet(context, id + "F14", {"entities" : qUnion([Q0, Q1, Q2, Q3, Q4, Q5]), "radius" : 3 * mm, "tangentPropagation" : true, "allowEdgeOverflow" : false});
        }
        {
            var Q0;
            Q0=makeQuery(id+"F1.opExtrude","CAP_EDGE",EDGE,{"disambiguationData":[OSD([sQuery(id+"F0.wireOp",EDGE,"E1.bottom")])],"isStart":false});
            fillet(context, id + "F15", {"entities" : qUnion([Q0]), "radius" : 2 * mm, "tangentPropagation" : true, "allowEdgeOverflow" : false});
        }
        {
            var Q0;
            {var subQ0=sQuery(id+"F0.wireOp",EDGE,"E1.bottom");var subQ1=sQuery(id+"F0.wireOp",EDGE,"E1.top");var subQ2=sQuery(id+"F0.wireOp",EDGE,"E1.left");var subQ3=sQuery(id+"F0.wireOp",EDGE,"E1.right");var subQ4=sQuery(id+"F0.wireOp",EDGE,"E4");var subQ5=sQuery(id+"F0.wireOp",EDGE,"E5");var subQ6=sQuery(id+"F0.wireOp",EDGE,"E6");var subQ7=sQuery(id+"F0.wireOp",EDGE,"E7");var subQ8=sQuery(id+"F0.wireOp",EDGE,"E21.filletArc");var subQ9=sQuery(id+"F0.wireOp",EDGE,"E22.filletArc");var subQ10=sQuery(id+"F0.wireOp",EDGE,"E23.filletArc");var subQ11=sQuery(id+"F0.wireOp",EDGE,"E24.filletArc");Q0=makeQuery(id+"F2.boolean.opBoolean","SPLIT",FACE,{"disambiguationData":[TD([makeQuery(id+"F1.opExtrude","SWEPT_FACE",FACE,{"disambiguationData":[OSD([subQ0])]})])],"derivedFrom":makeQuery(id+"F1.opExtrude","CAP_FACE",FACE,{"disambiguationData":[OSD([subQ0,subQ1,subQ2,subQ3,subQ4,subQ5,subQ6,subQ7,subQ8,subQ9,subQ10,subQ11])],"isStart":true})});}
            var sketch = newSketch(context, id + "F16", { "sketchPlane" : qUnion([Q0])});
            skLineSegment(sketch, "E79", {"start": v(94.05, 208.38) * mm, "end": v(94.05, 238.38) * mm, "construction": true});
            skArc(sketch, "E80", {"start": v(79.05, 238.38) * mm, "mid": v(94.05, 253.38) * mm, "end": v(109.05, 238.38) * mm});
            skCircle(sketch, "E81", {"center": v(94.05, 238.38) * mm, "radius": 6 * mm});
            skLineSegment(sketch, "E82", {"start": v(79.05, 238.38) * mm, "end": v(79.05, 226.38) * mm});
            skLineSegment(sketch, "E83", {"start": v(109.05, 238.38) * mm, "end": v(109.05, 226.38) * mm});
            skLineSegment(sketch, "E84", {"start": v(79.05, 226.38) * mm, "end": v(61.05, 208.38) * mm});
            skLineSegment(sketch, "E85", {"start": v(109.05, 226.38) * mm, "end": v(127.05, 208.38) * mm});
            skLineSegment(sketch, "E86", {"start": v(14.05, 118.38) * mm, "end": v(174.05, 118.38) * mm, "construction": true});
            skCircle(sketch, "E87.MirrorC", {"center": v(94.05, -1.62) * mm, "radius": 6 * mm});
            skLineSegment(sketch, "E88.MirrorCS", {"start": v(109.05, 10.38) * mm, "end": v(127.05, 28.38) * mm});
            skLineSegment(sketch, "E89.MirrorCS", {"start": v(109.05, -1.62) * mm, "end": v(109.05, 10.38) * mm});
            skArc(sketch, "E90.MirrorCS", {"start": v(79.05, -1.62) * mm, "mid": v(94.05, -16.62) * mm, "end": v(109.05, -1.62) * mm});
            skLineSegment(sketch, "E91.MirrorCS", {"start": v(79.05, -1.62) * mm, "end": v(79.05, 10.38) * mm});
            skLineSegment(sketch, "E92.MirrorCS", {"start": v(79.05, 10.38) * mm, "end": v(61.05, 28.38) * mm});
            skSolve(sketch);
        }
        {
            var Q0;
            Q0=makeQuery(id+"F16.imprint","IMPRINT",FACE,{"disambiguationData":[TD([[makeQuery(id+"F16.imprint","IMPRINT",EDGE,{"derivedFrom":makeQuery(id+"F1.opExtrude","CAP_EDGE",EDGE,{"disambiguationData":[OSD([sQuery(id+"F0.wireOp",EDGE,"E1.left")])],"isStart":true})}),-1.0]])]});
            var Q1;
            Q1=makeQuery(id+"F16.imprint","IMPRINT",FACE,{"disambiguationData":[TD([[makeQuery(id+"F16.imprint","IMPRINT",EDGE,{"derivedFrom":sQuery(id+"F16.wireOp",EDGE,"E87.MirrorC")}),1.0]])]});
            var Q2;
            Q2=makeQuery(id+"F16.imprint","IMPRINT",FACE,{"disambiguationData":[TD([[makeQuery(id+"F16.imprint","IMPRINT",EDGE,{"derivedFrom":sQuery(id+"F16.wireOp",EDGE,"E80")}),-1.0]])]});
            var Q3;
            Q3=makeQuery(id+"F2.opExtrude","CAP_FACE",FACE,{"disambiguationData":[OSD([sQuery(id+"F0.wireOp",EDGE,"E12"),sQuery(id+"F0.wireOp",EDGE,"E13"),sQuery(id+"F0.wireOp",EDGE,"E14"),sQuery(id+"F0.wireOp",EDGE,"E15"),sQuery(id+"F0.wireOp",EDGE,"E17.filletArc"),sQuery(id+"F0.wireOp",EDGE,"E18.filletArc"),sQuery(id+"F0.wireOp",EDGE,"E19.filletArc"),sQuery(id+"F0.wireOp",EDGE,"E20.filletArc"),sQuery(id+"F0.wireOp",EDGE,"E25.0"),sQuery(id+"F0.wireOp",EDGE,"E25.1"),sQuery(id+"F0.wireOp",EDGE,"E25.2"),sQuery(id+"F0.wireOp",EDGE,"E25.3"),sQuery(id+"F0.wireOp",EDGE,"E25.4"),sQuery(id+"F0.wireOp",EDGE,"E25.5"),sQuery(id+"F0.wireOp",EDGE,"E25.6"),sQuery(id+"F0.wireOp",EDGE,"E25.7")])],"isStart":false});
            extrude(context, id + "F17", {"entities" : qUnion([Q0, Q1, Q2]), "endBound" : BoundingType.UP_TO_SURFACE, "endBoundEntityFace" : qUnion([Q3]), "depth" : 25 * mm});
        }
    });
